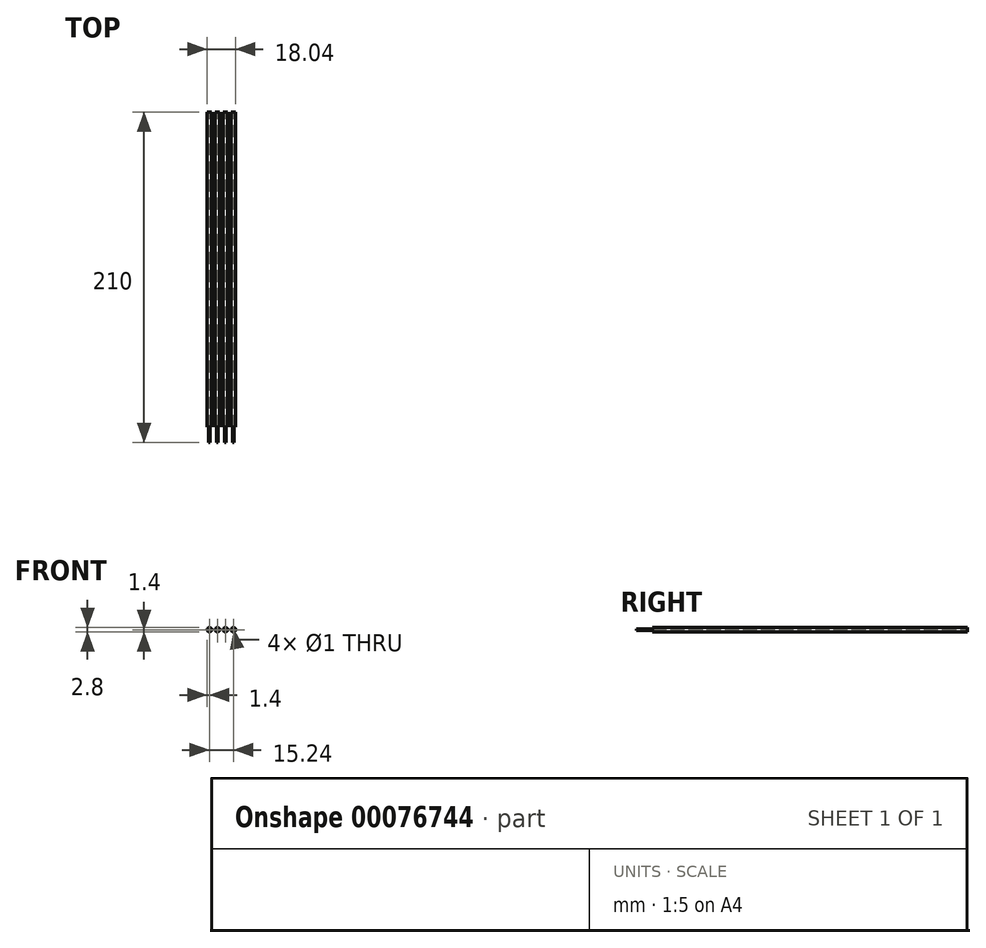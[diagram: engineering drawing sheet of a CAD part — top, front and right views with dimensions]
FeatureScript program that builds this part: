
annotation { "Feature Type Name" : "Feature", "Feature Type Description" : "" }
export const myFeature = defineFeature(function(context is Context, id is Id, definition is map)
    precondition{}
    {
        {
            var Q0;
            Q0=qCreatedBy(makeId("Front.planeOp"),FACE);
            var sketch = newSketch(context, id + "F0", { "sketchPlane" : qUnion([Q0])});
            skCircle(sketch, "E0", {"center": v(-7.62, 0) * mm, "radius": 1.4 * mm});
            skCircle(sketch, "E1.1.0.0", {"center": v(-2.54, 0) * mm, "radius": 1.4 * mm});
            skCircle(sketch, "E1.2.0.0", {"center": v(2.54, 0) * mm, "radius": 1.4 * mm});
            skCircle(sketch, "E1.3.0.0", {"center": v(7.62, 0) * mm, "radius": 1.4 * mm});
            skLineSegment(sketch, "E1.direction1", {"start": v(-7.62, 0) * mm, "end": v(-2.54, 0) * mm, "construction": true});
            skLineSegment(sketch, "E2", {"start": v(-2.54, 0) * mm, "end": v(2.54, 0) * mm, "construction": true});
            skLineSegment(sketch, "E3", {"start": v(2.54, 0) * mm, "end": v(7.62, 0) * mm, "construction": true});
            skCircle(sketch, "E4", {"center": v(-7.62, 0) * mm, "radius": 0.5 * mm});
            skCircle(sketch, "E5", {"center": v(-2.54, 0) * mm, "radius": 0.5 * mm});
            skCircle(sketch, "E6", {"center": v(2.54, 0) * mm, "radius": 0.5 * mm});
            skCircle(sketch, "E7", {"center": v(7.62, 0) * mm, "radius": 0.5 * mm});
            skSolve(sketch);
        }
        {
            var Q0;
            Q0=qSketchRegion(id+"F0",true);
            extrude(context, id + "F1", {"entities" : qUnion([Q0]), "depth" : 200 * mm});
        }
        {
            var Q0;
            Q0=makeQuery(id+"F0.imprint","IMPRINT",FACE,{"disambiguationData":[TD([[makeQuery(id+"F0.imprint","IMPRINT",EDGE,{"derivedFrom":sQuery(id+"F0.wireOp",EDGE,"E7")}),1.0]])]});
            var Q1;
            Q1=makeQuery(id+"F0.imprint","IMPRINT",FACE,{"disambiguationData":[TD([[makeQuery(id+"F0.imprint","IMPRINT",EDGE,{"derivedFrom":sQuery(id+"F0.wireOp",EDGE,"E6")}),1.0]])]});
            var Q2;
            Q2=makeQuery(id+"F0.imprint","IMPRINT",FACE,{"disambiguationData":[TD([[makeQuery(id+"F0.imprint","IMPRINT",EDGE,{"derivedFrom":sQuery(id+"F0.wireOp",EDGE,"E5")}),1.0]])]});
            var Q3;
            Q3=makeQuery(id+"F0.imprint","IMPRINT",FACE,{"disambiguationData":[TD([[makeQuery(id+"F0.imprint","IMPRINT",EDGE,{"derivedFrom":sQuery(id+"F0.wireOp",EDGE,"E4")}),1.0]])]});
            extrude(context, id + "F2", {"entities" : qUnion([Q0, Q1, Q2, Q3]), "depth" : 210 * mm});
        }
    });
